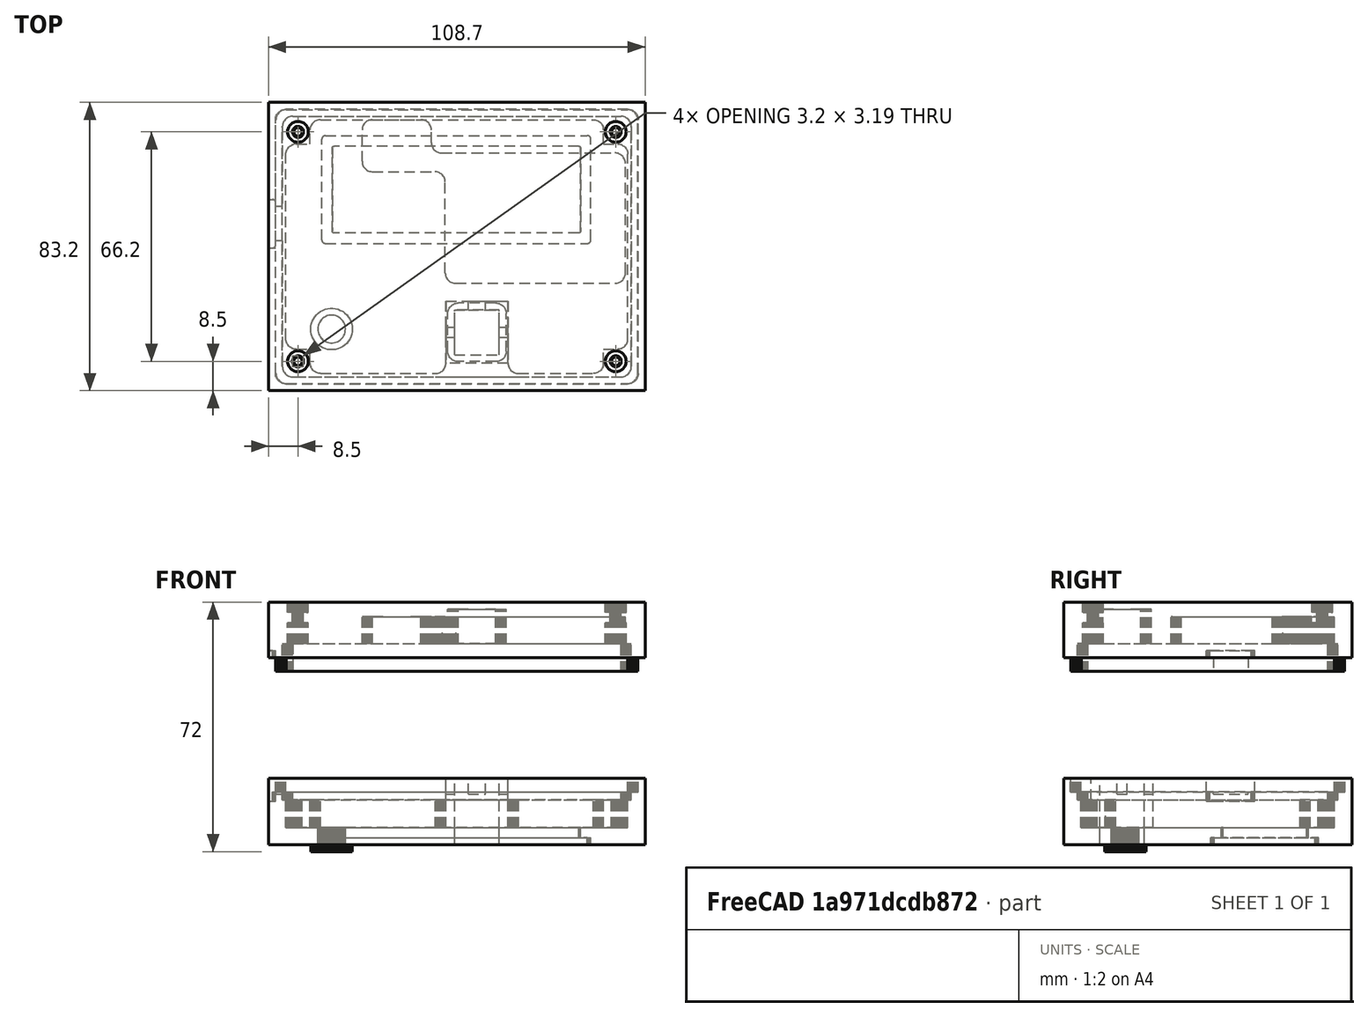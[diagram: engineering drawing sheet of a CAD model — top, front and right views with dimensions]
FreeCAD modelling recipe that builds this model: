
FCSTD DOCUMENT  (FreeCAD 0.16RUnknown)
Label: model
License: All rights reserved
LicenseURL: http://en.wikipedia.org/wiki/All_rights_reserved
objects: Part::Prism×77, Part::Box×44, Part::MultiFuse×22, Part::Cut×7
note: 150 computed .brp shape members not serialized (recipe doc carries the construction recipe); baked Part::Feature solids carry a one-line shape summary decoded from their .brp

FEATURE [Part::Box] cube
  Height = 20
  Length = 108.7
  Width = 83.2
FEATURE [Part::Box] cube001
  Height = 4
  Length = 108.7
  Width = 83.2
FEATURE [Part::Prism] prism
  Circumradius = 3
  Height = 4
  Placement = pos=(3,3,0) rot=(0,0,1;0rad)
  Polygon = 50
FEATURE [Part::Prism] prism001
  Circumradius = 3
  Height = 4
  Placement = pos=(101.5,3,0) rot=(0,0,1;0rad)
  Polygon = 50
FEATURE [Part::Prism] prism002
  Circumradius = 3
  Height = 4
  Placement = pos=(3,76,0) rot=(0,0,1;0rad)
  Polygon = 50
FEATURE [Part::Prism] prism003
  Circumradius = 3
  Height = 4
  Placement = pos=(101.5,76,0) rot=(0,0,1;0rad)
  Polygon = 50
FEATURE [Part::Box] cube002
  Height = 4
  Length = 98.5
  Placement = pos=(3,0,0) rot=(0,0,1;0rad)
  Width = 79
FEATURE [Part::Box] cube003
  Height = 4
  Length = 104.5
  Placement = pos=(0,3,0) rot=(0,0,1;0rad)
  Width = 73
FEATURE [Part::MultiFuse] union
  Placement = pos=(2.1,2.1,0) rot=(0,0,1;0rad)
  Shapes = -> [prism,prism001,prism002,prism003,cube002,cube003]
FEATURE [Part::Cut] difference
  Base = -> cube001
  Tool = -> union
FEATURE [Part::Prism] prism004
  Circumradius = 3
  Height = 8
  Placement = pos=(3,3,0) rot=(0,0,1;0rad)
  Polygon = 50
FEATURE [Part::Prism] prism005
  Circumradius = 3
  Height = 8
  Placement = pos=(97.7,3,0) rot=(0,0,1;0rad)
  Polygon = 50
FEATURE [Part::Prism] prism006
  Circumradius = 3
  Height = 8
  Placement = pos=(3,72.2,0) rot=(0,0,1;0rad)
  Polygon = 50
FEATURE [Part::Prism] prism007
  Circumradius = 3
  Height = 8
  Placement = pos=(97.7,72.2,0) rot=(0,0,1;0rad)
  Polygon = 50
FEATURE [Part::Box] cube004
  Height = 8
  Length = 94.7
  Placement = pos=(3,0,0) rot=(0,0,1;0rad)
  Width = 75.2
FEATURE [Part::Box] cube005
  Height = 8
  Length = 100.7
  Placement = pos=(0,3,0) rot=(0,0,1;0rad)
  Width = 69.2
FEATURE [Part::MultiFuse] union001
  Placement = pos=(4,4,0) rot=(0,0,1;0rad)
  Shapes = -> [prism004,prism005,prism006,prism007,cube004,cube005]
FEATURE [Part::Prism] prism008
  Circumradius = 3
  Height = 18
  Placement = pos=(3,3,0) rot=(0,0,1;0rad)
  Polygon = 50
FEATURE [Part::Prism] prism009
  Circumradius = 3
  Height = 18
  Placement = pos=(13.9,3,0) rot=(0,0,1;0rad)
  Polygon = 50
FEATURE [Part::Prism] prism010
  Circumradius = 3
  Height = 18
  Placement = pos=(3,13.9,0) rot=(0,0,1;0rad)
  Polygon = 50
FEATURE [Part::Prism] prism011
  Circumradius = 3
  Height = 18
  Placement = pos=(13.9,13.9,0) rot=(0,0,1;0rad)
  Polygon = 50
FEATURE [Part::Box] cube006
  Height = 18
  Length = 10.9
  Placement = pos=(3,0,0) rot=(0,0,1;0rad)
  Width = 16.9
FEATURE [Part::Box] cube007
  Height = 18
  Length = 16.9
  Placement = pos=(0,3,0) rot=(0,0,1;0rad)
  Width = 10.9
FEATURE [Part::MultiFuse] union002
  Placement = pos=(51.7,8.4,0) rot=(0,0,1;0rad)
  Shapes = -> [prism008,prism009,prism010,prism011,cube006,cube007]
FEATURE [Part::Prism] prism012
  Circumradius = 3
  Height = 7.8
  Placement = pos=(3,3,0) rot=(0,0,1;0rad)
  Polygon = 50
FEATURE [Part::Prism] prism013
  Circumradius = 3
  Height = 7.8
  Placement = pos=(49,3,0) rot=(0,0,1;0rad)
  Polygon = 50
FEATURE [Part::Prism] prism014
  Circumradius = 3
  Height = 7.8
  Placement = pos=(3,34.6,0) rot=(0,0,1;0rad)
  Polygon = 50
FEATURE [Part::Prism] prism015
  Circumradius = 3
  Height = 7.8
  Placement = pos=(49,34.6,0) rot=(0,0,1;0rad)
  Polygon = 50
FEATURE [Part::Box] cube008
  Height = 7.8
  Length = 46
  Placement = pos=(3,0,0) rot=(0,0,1;0rad)
  Width = 37.6
FEATURE [Part::Box] cube009
  Height = 7.8
  Length = 52
  Placement = pos=(0,3,0) rot=(0,0,1;0rad)
  Width = 31.6
FEATURE [Part::MultiFuse] union003
  Placement = pos=(51,31,8) rot=(0,0,1;0rad)
  Shapes = -> [prism012,prism013,prism014,prism015,cube008,cube009]
FEATURE [Part::Prism] prism016
  Circumradius = 3
  Height = 7.8
  Placement = pos=(3,3,0) rot=(0,0,1;0rad)
  Polygon = 50
FEATURE [Part::Prism] prism017
  Circumradius = 3
  Height = 7.8
  Placement = pos=(17,3,0) rot=(0,0,1;0rad)
  Polygon = 50
FEATURE [Part::Prism] prism018
  Circumradius = 3
  Height = 7.8
  Placement = pos=(3,12,0) rot=(0,0,1;0rad)
  Polygon = 50
FEATURE [Part::Prism] prism019
  Circumradius = 3
  Height = 7.8
  Placement = pos=(17,12,0) rot=(0,0,1;0rad)
  Polygon = 50
FEATURE [Part::Box] cube010
  Height = 7.8
  Length = 14
  Placement = pos=(3,0,0) rot=(0,0,1;0rad)
  Width = 15
FEATURE [Part::Box] cube011
  Height = 7.8
  Length = 20
  Placement = pos=(0,3,0) rot=(0,0,1;0rad)
  Width = 9
FEATURE [Part::MultiFuse] union004
  Placement = pos=(27,63.2,8) rot=(0,0,1;0rad)
  Shapes = -> [prism016,prism017,prism018,prism019,cube010,cube011]
FEATURE [Part::Box] cube012
  Height = 7.8
  Length = 15
  Placement = pos=(44,63.2,8) rot=(0,0,1;0rad)
  Width = 5.4
FEATURE [Part::Box] cube013
  Height = 7.8
  Length = 3
  Width = 3
FEATURE [Part::Prism] prism020
  Circumradius = 3
  Height = 7.8
  Polygon = 50
FEATURE [Part::Cut] difference001
  Base = -> cube013
  Placement = pos=(48,60.2,8) rot=(0,0,1;0rad)
  Tool = -> prism020
FEATURE [Part::Box] cube014
  Height = 7.8
  Length = 3
  Placement = pos=(-3,-3,0) rot=(0,0,1;0rad)
  Width = 3
FEATURE [Part::Prism] prism021
  Circumradius = 3
  Height = 7.8
  Polygon = 50
FEATURE [Part::Cut] difference002
  Base = -> cube014
  Placement = pos=(50,71.599,8) rot=(0,0,1;0rad)
  Tool = -> prism021
FEATURE [Part::Box] cube015
  Height = 4
  Length = 4
  Placement = pos=(0,43.2,0) rot=(0,0,1;0rad)
  Width = 10
FEATURE [Part::Prism] prism022
  Circumradius = 1
  Height = 6
  Placement = pos=(1,1,0) rot=(0,0,1;0rad)
  Polygon = 50
FEATURE [Part::Prism] prism023
  Circumradius = 1
  Height = 6
  Placement = pos=(3.2,1,0) rot=(0,0,1;0rad)
  Polygon = 50
FEATURE [Part::Prism] prism024
  Circumradius = 1
  Height = 6
  Placement = pos=(1,13,0) rot=(0,0,1;0rad)
  Polygon = 50
FEATURE [Part::Prism] prism025
  Circumradius = 1
  Height = 6
  Placement = pos=(3.2,13,0) rot=(0,0,1;0rad)
  Polygon = 50
FEATURE [Part::Box] cube016
  Height = 6
  Length = 2.2
  Placement = pos=(1,0,0) rot=(0,0,1;0rad)
  Width = 14
FEATURE [Part::Box] cube017
  Height = 6
  Length = 4.2
  Placement = pos=(0,1,0) rot=(0,0,1;0rad)
  Width = 12
FEATURE [Part::MultiFuse] union005
  Placement = pos=(-2.1,41.2,0) rot=(0,0,1;0rad)
  Shapes = -> [prism022,prism023,prism024,prism025,cube016,cube017]
FEATURE [Part::Prism] prism026
  Circumradius = 3
  Height = 3
  Placement = pos=(0,0,17) rot=(0,0,1;0rad)
  Polygon = 50
FEATURE [Part::Prism] prism027
  Circumradius = 1.6
  Height = 3
  Placement = pos=(0,0,14) rot=(0,0,1;0rad)
  Polygon = 50
FEATURE [Part::Prism] prism028
  Circumradius = 3
  Height = 14
  Polygon = 50
FEATURE [Part::MultiFuse] Group
  Placement = pos=(8.5,8.5,0) rot=(0,0,1;0rad)
  Shapes = -> [prism026,prism027,prism028]
FEATURE [Part::Prism] prism029
  Circumradius = 3
  Height = 3
  Placement = pos=(0,0,17) rot=(0,0,1;0rad)
  Polygon = 50
FEATURE [Part::Prism] prism030
  Circumradius = 1.6
  Height = 3
  Placement = pos=(0,0,14) rot=(0,0,1;0rad)
  Polygon = 50
FEATURE [Part::Prism] prism031
  Circumradius = 3
  Height = 14
  Polygon = 50
FEATURE [Part::MultiFuse] Group001
  Placement = pos=(100.2,8.5,0) rot=(0,0,1;0rad)
  Shapes = -> [prism029,prism030,prism031]
FEATURE [Part::Prism] prism032
  Circumradius = 3
  Height = 3
  Placement = pos=(0,0,17) rot=(0,0,1;0rad)
  Polygon = 50
FEATURE [Part::Prism] prism033
  Circumradius = 1.6
  Height = 3
  Placement = pos=(0,0,14) rot=(0,0,1;0rad)
  Polygon = 50
FEATURE [Part::Prism] prism034
  Circumradius = 3
  Height = 14
  Polygon = 50
FEATURE [Part::MultiFuse] Group002
  Placement = pos=(8.5,74.7,0) rot=(0,0,1;0rad)
  Shapes = -> [prism032,prism033,prism034]
FEATURE [Part::Prism] prism035
  Circumradius = 3
  Height = 3
  Placement = pos=(0,0,17) rot=(0,0,1;0rad)
  Polygon = 50
FEATURE [Part::Prism] prism036
  Circumradius = 1.6
  Height = 3
  Placement = pos=(0,0,14) rot=(0,0,1;0rad)
  Polygon = 50
FEATURE [Part::Prism] prism037
  Circumradius = 3
  Height = 14
  Polygon = 50
FEATURE [Part::MultiFuse] Group003
  Placement = pos=(100.2,74.7,0) rot=(0,0,1;0rad)
  Shapes = -> [prism035,prism036,prism037]
FEATURE [Part::MultiFuse] union006
  Shapes = -> [difference,union001,union002,union003,union004,cube012,difference001,difference002,cube015,union005,Group,Group001,Group002,Group003]
FEATURE [Part::Cut] difference003
  Base = -> cube
  Placement = pos=(0,0,50) rot=(0,0,1;0rad)
  Tool = -> union006
FEATURE [Part::Box] cube018
  Height = 17.2
  Length = 17.9
  Placement = pos=(-2.5,-6.4,2) rot=(0,0,1;0rad)
  Width = 21.8
FEATURE [Part::Box] cube019
  Height = 13.2
  Length = 23.9
  Placement = pos=(-5.5,-6.4,2) rot=(0,0,1;0rad)
  Width = 3
FEATURE [Part::Box] cube020
  Height = 11
  Length = 23.9
  Placement = pos=(-5.5,-5.4,2) rot=(0,0,1;0rad)
  Width = 3
FEATURE [Part::MultiFuse] union007
  Shapes = -> [cube018,cube019,cube020]
FEATURE [Part::Prism] prism038
  Circumradius = 3
  Height = 13
  Placement = pos=(-5.5,-2.4,0) rot=(0,0,1;0rad)
  Polygon = 50
FEATURE [Part::Prism] prism039
  Circumradius = 3
  Height = 13
  Placement = pos=(18.4,-2.4,0) rot=(0,0,1;0rad)
  Polygon = 50
FEATURE [Part::Prism] prism040
  Circumradius = 3
  Height = 15.2
  Placement = pos=(-5.5,-3.4,13) rot=(0,0,1;0rad)
  Polygon = 50
FEATURE [Part::Prism] prism041
  Circumradius = 3
  Height = 15.2
  Placement = pos=(18.4,-3.4,13) rot=(0,0,1;0rad)
  Polygon = 50
FEATURE [Part::Box] cube021
  Height = 19.2
  Length = 12.9
  Width = 12.9
FEATURE [Part::Box] cube022
  Height = 15.2
  Length = 2.5
  Placement = pos=(-2.5,4.95,14.6) rot=(0,0,1;0rad)
  Width = 3
FEATURE [Part::Box] cube023
  Height = 15.2
  Length = 2.5
  Placement = pos=(12.9,4.95,14.6) rot=(0,0,1;0rad)
  Width = 3
FEATURE [Part::Box] cube024
  Height = 15.2
  Length = 5
  Placement = pos=(3.95,12.9,14.6) rot=(0,0,1;0rad)
  Width = 2.5
FEATURE [Part::Box] cube025
  Height = 13.2
  Length = 23.9
  Placement = pos=(-5.5,-10.4,13) rot=(0,0,1;0rad)
  Width = 7.9
FEATURE [Part::MultiFuse] union008
  Shapes = -> [prism038,prism039,prism040,prism041,cube021,cube022,cube023,cube024,cube025]
FEATURE [Part::Cut] difference004
  Base = -> union007
  Placement = pos=(53.7,10.4,0) rot=(0,0,1;0rad)
  Tool = -> union008
FEATURE [Part::Box] cube026
  Height = 19.2
  Length = 108.7
  Width = 83.2
FEATURE [Part::Prism] prism042
  Circumradius = 3
  Height = 19.2
  Placement = pos=(3,3,0) rot=(0,0,1;0rad)
  Polygon = 50
FEATURE [Part::Prism] prism043
  Circumradius = 3
  Height = 19.2
  Placement = pos=(97.7,3,0) rot=(0,0,1;0rad)
  Polygon = 50
FEATURE [Part::Prism] prism044
  Circumradius = 3
  Height = 19.2
  Placement = pos=(3,72.2,0) rot=(0,0,1;0rad)
  Polygon = 50
FEATURE [Part::Prism] prism045
  Circumradius = 3
  Height = 19.2
  Placement = pos=(97.7,72.2,0) rot=(0,0,1;0rad)
  Polygon = 50
FEATURE [Part::Box] cube027
  Height = 19.2
  Length = 94.7
  Placement = pos=(3,0,0) rot=(0,0,1;0rad)
  Width = 75.2
FEATURE [Part::Box] cube028
  Height = 19.2
  Length = 100.7
  Placement = pos=(0,3,0) rot=(0,0,1;0rad)
  Width = 69.2
FEATURE [Part::MultiFuse] union009
  Placement = pos=(4,4,13) rot=(0,0,1;0rad)
  Shapes = -> [prism042,prism043,prism044,prism045,cube027,cube028]
FEATURE [Part::Prism] prism046
  Circumradius = 3
  Height = 19.2
  Placement = pos=(3,3,0) rot=(0,0,1;0rad)
  Polygon = 50
FEATURE [Part::Prism] prism047
  Circumradius = 3
  Height = 19.2
  Placement = pos=(81.7,3,0) rot=(0,0,1;0rad)
  Polygon = 50
FEATURE [Part::Prism] prism048
  Circumradius = 3
  Height = 19.2
  Placement = pos=(3,70.2,0) rot=(0,0,1;0rad)
  Polygon = 50
FEATURE [Part::Prism] prism049
  Circumradius = 3
  Height = 19.2
  Placement = pos=(81.7,70.2,0) rot=(0,0,1;0rad)
  Polygon = 50
FEATURE [Part::Box] cube029
  Height = 19.2
  Length = 78.7
  Placement = pos=(3,0,0) rot=(0,0,1;0rad)
  Width = 73.2
FEATURE [Part::Box] cube030
  Height = 19.2
  Length = 84.7
  Placement = pos=(0,3,0) rot=(0,0,1;0rad)
  Width = 67.2
FEATURE [Part::MultiFuse] union010
  Placement = pos=(12,5,5) rot=(0,0,1;0rad)
  Shapes = -> [prism046,prism047,prism048,prism049,cube029,cube030]
FEATURE [Part::Prism] prism050
  Circumradius = 3
  Height = 19.2
  Placement = pos=(3,3,0) rot=(0,0,1;0rad)
  Polygon = 50
FEATURE [Part::Prism] prism051
  Circumradius = 3
  Height = 19.2
  Placement = pos=(95.7,3,0) rot=(0,0,1;0rad)
  Polygon = 50
FEATURE [Part::Prism] prism052
  Circumradius = 3
  Height = 19.2
  Placement = pos=(3,56.2,0) rot=(0,0,1;0rad)
  Polygon = 50
FEATURE [Part::Prism] prism053
  Circumradius = 3
  Height = 19.2
  Placement = pos=(95.7,56.2,0) rot=(0,0,1;0rad)
  Polygon = 50
FEATURE [Part::Box] cube031
  Height = 19.2
  Length = 92.7
  Placement = pos=(3,0,0) rot=(0,0,1;0rad)
  Width = 59.2
FEATURE [Part::Box] cube032
  Height = 19.2
  Length = 98.7
  Placement = pos=(0,3,0) rot=(0,0,1;0rad)
  Width = 53.2
FEATURE [Part::MultiFuse] union011
  Placement = pos=(5,12,5) rot=(0,0,1;0rad)
  Shapes = -> [prism050,prism051,prism052,prism053,cube031,cube032]
FEATURE [Part::Prism] prism054
  Circumradius = 3
  Height = 19.2
  Placement = pos=(3,3,0) rot=(0,0,1;0rad)
  Polygon = 50
FEATURE [Part::Prism] prism055
  Circumradius = 3
  Height = 19.2
  Placement = pos=(101.7,3,0) rot=(0,0,1;0rad)
  Polygon = 50
FEATURE [Part::Prism] prism056
  Circumradius = 3
  Height = 19.2
  Placement = pos=(3,76.2,0) rot=(0,0,1;0rad)
  Polygon = 50
FEATURE [Part::Prism] prism057
  Circumradius = 3
  Height = 19.2
  Placement = pos=(101.7,76.2,0) rot=(0,0,1;0rad)
  Polygon = 50
FEATURE [Part::Box] cube033
  Height = 19.2
  Length = 98.7
  Placement = pos=(3,0,0) rot=(0,0,1;0rad)
  Width = 79.2
FEATURE [Part::Box] cube034
  Height = 19.2
  Length = 104.7
  Placement = pos=(0,3,0) rot=(0,0,1;0rad)
  Width = 73.2
FEATURE [Part::MultiFuse] union012
  Placement = pos=(2,2,15.2) rot=(0,0,1;0rad)
  Shapes = -> [prism054,prism055,prism056,prism057,cube033,cube034]
FEATURE [Part::Prism] prism058
  Circumradius = 1.2
  Height = 19.2
  Placement = pos=(8.5,8.5,5) rot=(0,0,1;0rad)
  Polygon = 50
FEATURE [Part::Prism] prism059
  Circumradius = 1.2
  Height = 19.2
  Placement = pos=(100.2,8.5,5) rot=(0,0,1;0rad)
  Polygon = 50
FEATURE [Part::Prism] prism060
  Circumradius = 1.2
  Height = 19.2
  Placement = pos=(8.5,74.7,5) rot=(0,0,1;0rad)
  Polygon = 50
FEATURE [Part::Prism] prism061
  Circumradius = 1.2
  Height = 19.2
  Placement = pos=(100.2,74.7,5) rot=(0,0,1;0rad)
  Polygon = 50
FEATURE [Part::Prism] prism062
  Circumradius = 4
  Height = 5
  Placement = pos=(18.2,17.8,0) rot=(0,0,1;0rad)
  Polygon = 50
FEATURE [Part::Prism] prism063
  Circumradius = 0.5
  Height = 25.1
  Placement = pos=(0.5,0.5,0) rot=(0,0,1;0rad)
  Polygon = 50
FEATURE [Part::Prism] prism064
  Circumradius = 0.5
  Height = 25.1
  Placement = pos=(71.1,0.5,0) rot=(0,0,1;0rad)
  Polygon = 50
FEATURE [Part::Prism] prism065
  Circumradius = 0.5
  Height = 25.1
  Placement = pos=(0.5,24.6,0) rot=(0,0,1;0rad)
  Polygon = 50
FEATURE [Part::Prism] prism066
  Circumradius = 0.5
  Height = 25.1
  Placement = pos=(71.1,24.6,0) rot=(0,0,1;0rad)
  Polygon = 50
FEATURE [Part::Box] cube035
  Height = 25.1
  Length = 70.6
  Placement = pos=(0.5,0,0) rot=(0,0,1;0rad)
  Width = 25.1
FEATURE [Part::Box] cube036
  Height = 25.1
  Length = 71.6
  Placement = pos=(0,0.5,0) rot=(0,0,1;0rad)
  Width = 24.1
FEATURE [Part::MultiFuse] union013
  Placement = pos=(18.4,45.5,0) rot=(0,0,1;0rad)
  Shapes = -> [prism063,prism064,prism065,prism066,cube035,cube036]
FEATURE [Part::Box] cube037
  Height = 19.2
  Length = 12.9
  Placement = pos=(53.7,10.4,0) rot=(0,0,1;0rad)
  Width = 12.9
FEATURE [Part::Prism] prism067
  Circumradius = 1
  Height = 2
  Placement = pos=(1,1,0) rot=(0,0,1;0rad)
  Polygon = 50
FEATURE [Part::Prism] prism068
  Circumradius = 1
  Height = 2
  Placement = pos=(76.6,1,0) rot=(0,0,1;0rad)
  Polygon = 50
FEATURE [Part::Prism] prism069
  Circumradius = 1
  Height = 2
  Placement = pos=(1,30.1,0) rot=(0,0,1;0rad)
  Polygon = 50
FEATURE [Part::Prism] prism070
  Circumradius = 1
  Height = 2
  Placement = pos=(76.6,30.1,0) rot=(0,0,1;0rad)
  Polygon = 50
FEATURE [Part::Box] cube038
  Height = 2
  Length = 75.6
  Placement = pos=(1,0,0) rot=(0,0,1;0rad)
  Width = 31.1
FEATURE [Part::Box] cube039
  Height = 2
  Length = 77.6
  Placement = pos=(0,1,0) rot=(0,0,1;0rad)
  Width = 29.1
FEATURE [Part::MultiFuse] union014
  Placement = pos=(15.4,42.5,0) rot=(0,0,1;0rad)
  Shapes = -> [prism067,prism068,prism069,prism070,cube038,cube039]
FEATURE [Part::Box] cube040
  Height = 4.6
  Length = 4
  Placement = pos=(0,43.2,14.6) rot=(0,0,1;0rad)
  Width = 10
FEATURE [Part::Prism] prism071
  Circumradius = 1
  Height = 6.6
  Placement = pos=(1,1,0) rot=(0,0,1;0rad)
  Polygon = 50
FEATURE [Part::Prism] prism072
  Circumradius = 1
  Height = 6.6
  Placement = pos=(3.2,1,0) rot=(0,0,1;0rad)
  Polygon = 50
FEATURE [Part::Prism] prism073
  Circumradius = 1
  Height = 6.6
  Placement = pos=(1,13,0) rot=(0,0,1;0rad)
  Polygon = 50
FEATURE [Part::Prism] prism074
  Circumradius = 1
  Height = 6.6
  Placement = pos=(3.2,13,0) rot=(0,0,1;0rad)
  Polygon = 50
FEATURE [Part::Box] cube041
  Height = 6.6
  Length = 2.2
  Placement = pos=(1,0,0) rot=(0,0,1;0rad)
  Width = 14
FEATURE [Part::Box] cube042
  Height = 6.6
  Length = 4.2
  Placement = pos=(0,1,0) rot=(0,0,1;0rad)
  Width = 12
FEATURE [Part::MultiFuse] union015
  Placement = pos=(-2.1,41.2,12.6) rot=(0,0,1;0rad)
  Shapes = -> [prism071,prism072,prism073,prism074,cube041,cube042]
FEATURE [Part::Box] cube043
  Height = 4
  Length = 2.1
  Placement = pos=(0,41.2,15.2) rot=(0,0,1;0rad)
  Width = 14
FEATURE [Part::MultiFuse] union016
  Shapes = -> [union009,union010,union011,union012,prism058,prism059,prism060,prism061,prism062,union013,cube037,union014,cube040,union015,cube043]
FEATURE [Part::Cut] difference005
  Base = -> cube026
  Tool = -> union016
FEATURE [Part::Prism] prism075
  Circumradius = 6
  Height = 4
  Placement = pos=(18.2,17.8,-2) rot=(0,0,1;0rad)
  Polygon = 50
FEATURE [Part::Prism] prism076
  Circumradius = 4
  Height = 4
  Placement = pos=(18.2,17.8,-2) rot=(0,0,1;0rad)
  Polygon = 50
FEATURE [Part::Cut] difference006
  Base = -> prism075
  Tool = -> prism076
FEATURE [Part::MultiFuse] Group004
  Shapes = -> [difference003,difference004,difference005,difference006]
